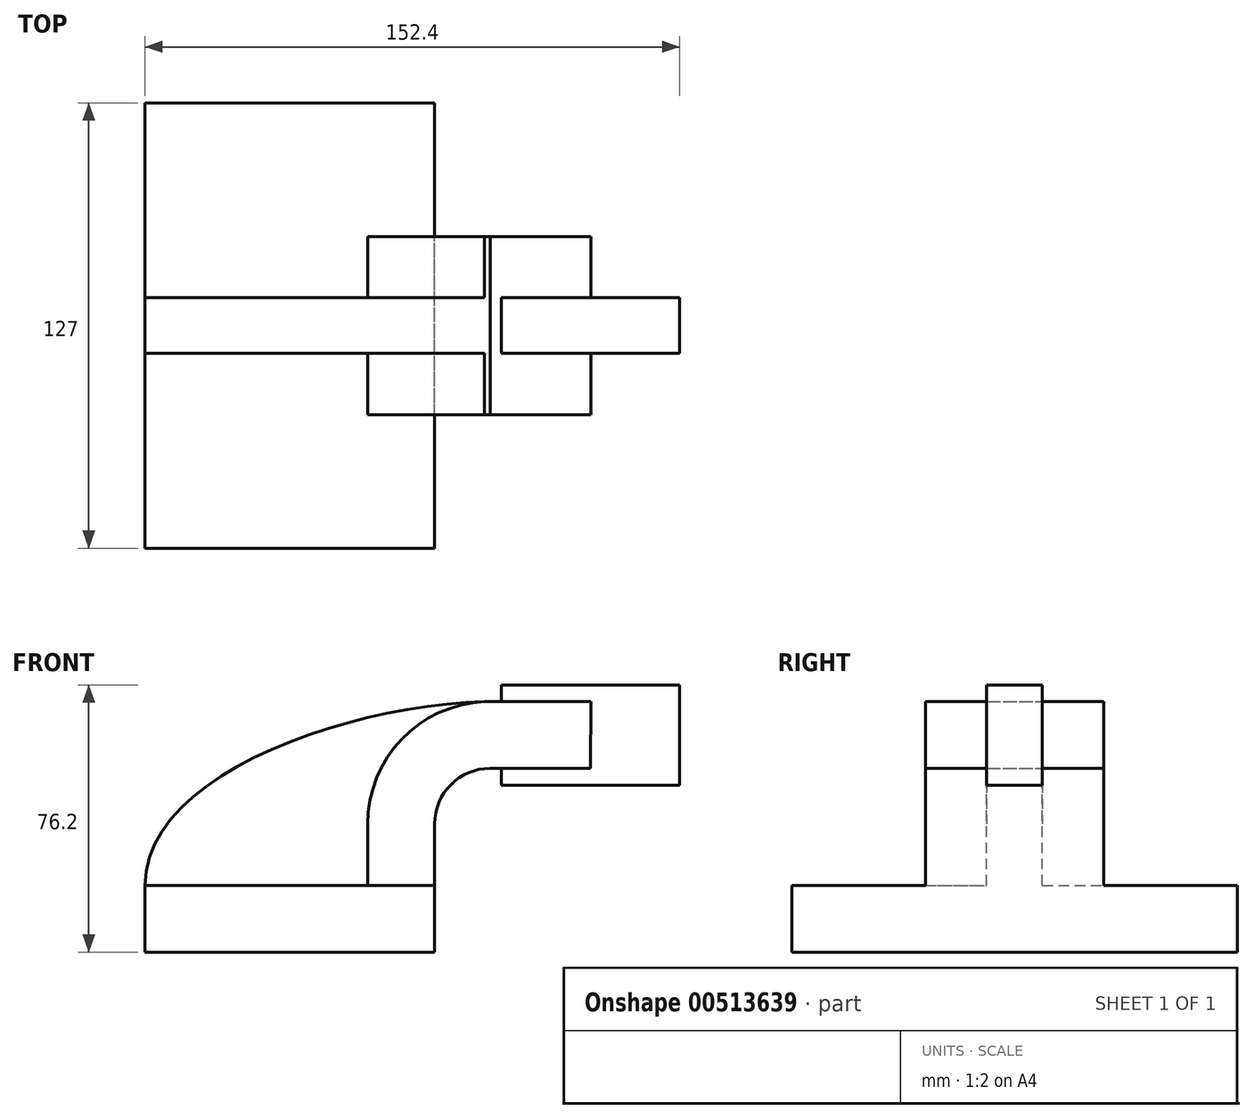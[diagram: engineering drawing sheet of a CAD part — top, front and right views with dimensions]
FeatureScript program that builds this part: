
annotation { "Feature Type Name" : "Feature", "Feature Type Description" : "" }
export const myFeature = defineFeature(function(context is Context, id is Id, definition is map)
    precondition{}
    {
        {
            var Q0;
            Q0=qCreatedBy(makeId("Front.planeOp"),FACE);
            var sketch = newSketch(context, id + "F0", { "sketchPlane" : qUnion([Q0])});
            skLineSegment(sketch, "E0.bottom", {"start": v(41.27, 9.52) * mm, "end": v(-41.28, 9.53) * mm});
            skLineSegment(sketch, "E0.top", {"start": v(41.28, -9.53) * mm, "end": v(-41.28, -9.52) * mm});
            skLineSegment(sketch, "E0.left", {"start": v(41.28, 9.52) * mm, "end": v(41.28, -9.53) * mm});
            skLineSegment(sketch, "E0.right", {"start": v(-41.28, 9.53) * mm, "end": v(-41.28, -9.52) * mm});
            skPoint(sketch, "E0.middle", {"position": v(0, 0) * mm});
            skLineSegment(sketch, "E1.bottom", {"start": v(60.32, 38.1) * mm, "end": v(111.12, 38.1) * mm});
            skLineSegment(sketch, "E1.top", {"start": v(60.32, 66.68) * mm, "end": v(111.12, 66.68) * mm});
            skLineSegment(sketch, "E1.left", {"start": v(60.32, 38.1) * mm, "end": v(60.32, 66.68) * mm});
            skLineSegment(sketch, "E1.right", {"start": v(111.13, 38.1) * mm, "end": v(111.12, 66.68) * mm});
            skPoint(sketch, "E1.middle", {"position": v(85.72, 52.39) * mm});
            skLineSegment(sketch, "E2", {"start": v(41.28, 9.52) * mm, "end": v(41.28, 27) * mm});
            skLineSegment(sketch, "E3", {"start": v(57.15, 42.88) * mm, "end": v(85.86, 42.88) * mm});
            skPoint(sketch, "E4.visualSharp", {"position": v(41.27, 42.88) * mm});
            skArc(sketch, "E4.filletArc", {"start": v(57.15, 42.88) * mm, "mid": v(45.92, 38.23) * mm, "end": v(41.27, 27) * mm});
            skLineSegment(sketch, "E5.0", {"start": v(57.15, 61.93) * mm, "end": v(85.86, 61.93) * mm});
            skArc(sketch, "E5.1", {"start": v(57.15, 61.93) * mm, "mid": v(32.45, 51.7) * mm, "end": v(22.23, 27) * mm});
            skLineSegment(sketch, "E5.2", {"start": v(22.22, 9.52) * mm, "end": v(22.22, 27) * mm});
            skLineSegment(sketch, "E6", {"start": v(85.72, 38.1) * mm, "end": v(85.86, 66.68) * mm});
            skFitSpline(sketch, "E7", {"points": [v(-41.28, 9.53) * mm, v(57.15, 61.93) * mm], "startDerivative": vector(0.63, 95.96) * mm, "endDerivative": vector(120.15, 2.05) * mm});
            skSolve(sketch);
        }
        {
            var Q0;
            Q0=makeQuery(id+"F0.imprint","IMPRINT",FACE,{"disambiguationData":[TD([[makeQuery(id+"F0.imprint","IMPRINT",EDGE,{"derivedFrom":sQuery(id+"F0.wireOp",EDGE,"E0.top")}),-1.0]])]});
            extrude(context, id + "F1", {"entities" : qUnion([Q0]), "endBound" : BoundingType.SYMMETRIC, "depth" : 127 * mm, "offsetDistance" : 25.4 * mm});
        }
        {
            var Q0;
            {var subQ4=sQuery(id+"F0.wireOp",EDGE,"E2");Q0=makeQuery(id+"F0.imprint","IMPRINT",FACE,{"disambiguationData":[TD([[makeQuery(id+"F0.imprint","IMPRINT",EDGE,{"derivedFrom":subQ4}),1.0]])]});}
            var Q1;
            {var subQ0=sQuery(id+"F0.wireOp",EDGE,"E3");var subQ1=sQuery(id+"F0.wireOp",EDGE,"E1.left");var subQ2=makeQuery(id+"F0.imprint","INTERSECT",VERTEX,{"derivedFrom":[subQ1,subQ0]});Q1=makeQuery(id+"F0.imprint","IMPRINT",FACE,{"disambiguationData":[TD([[makeQuery(id+"F0.imprint","IMPRINT",EDGE,{"disambiguationData":[TD([[subQ2,-1.0]])],"derivedFrom":subQ1}),-1.0]])]});}
            extrude(context, id + "F2", {"entities" : qUnion([Q0, Q1]), "operationType" : NewBodyOperationType.ADD, "endBound" : BoundingType.SYMMETRIC, "depth" : 50.8 * mm, "offsetDistance" : 25.4 * mm});
        }
        {
            var Q0;
            Q0 = qSketchRegion(id + "F0", true);
            extrude(context, id + "F3", {"entities" : qUnion([Q0]), "operationType" : NewBodyOperationType.ADD, "endBound" : BoundingType.SYMMETRIC, "depth" : 15.88 * mm, "offsetDistance" : 25.4 * mm});
        }
    });
